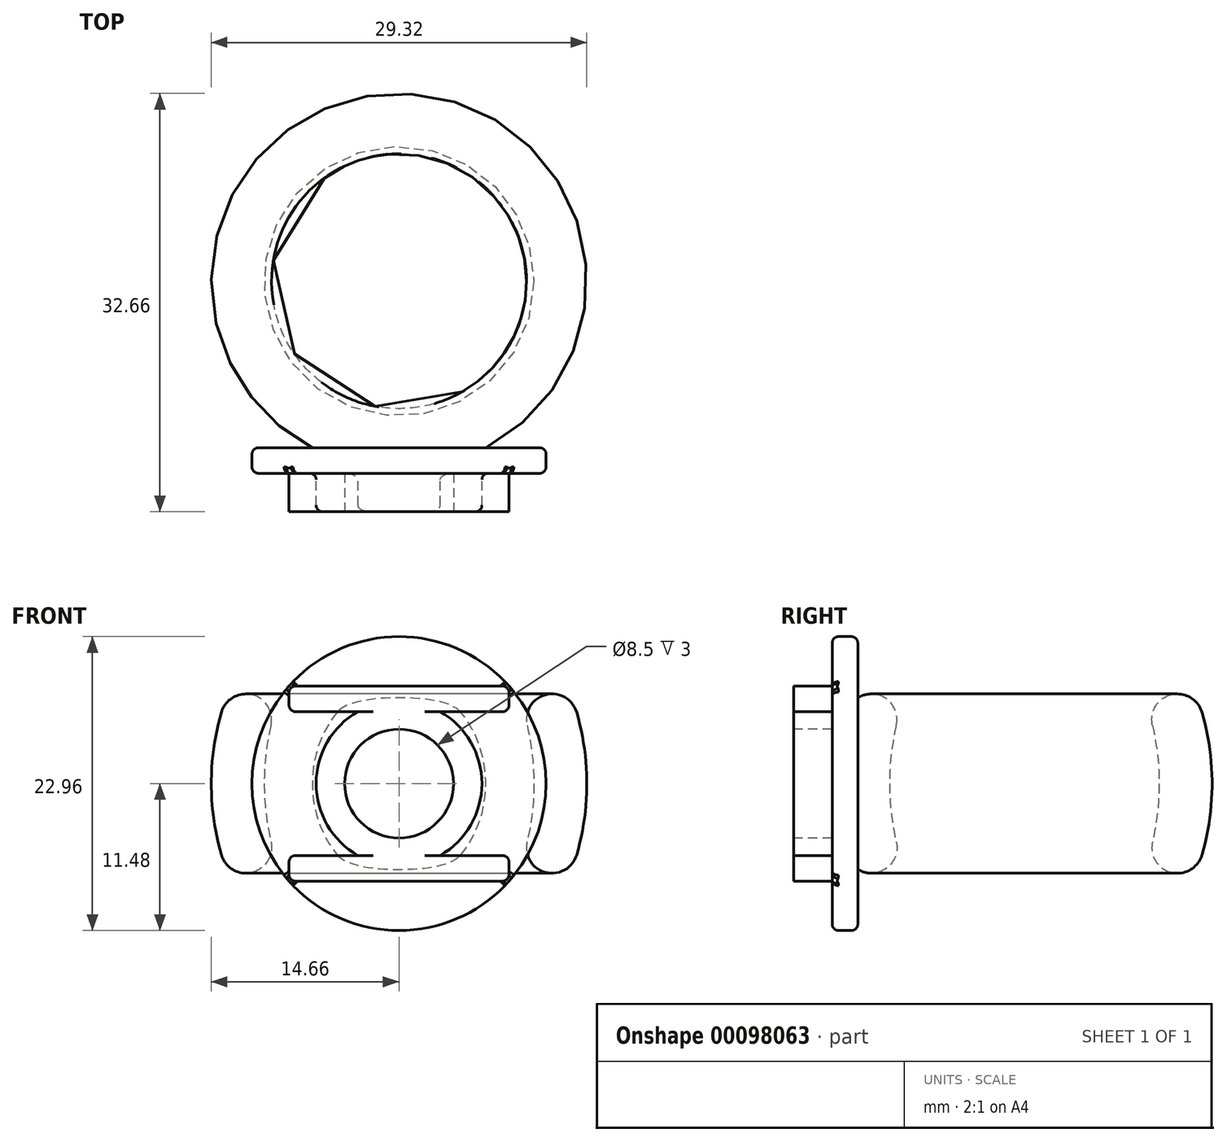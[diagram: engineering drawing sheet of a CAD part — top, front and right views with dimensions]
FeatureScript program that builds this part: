
annotation { "Feature Type Name" : "Feature", "Feature Type Description" : "" }
export const myFeature = defineFeature(function(context is Context, id is Id, definition is map)
    precondition{}
    {
        {
            var Q0;
            Q0=qCreatedBy(makeId("Front.planeOp"),FACE);
            var sketch = newSketch(context, id + "F0", { "sketchPlane" : qUnion([Q0])});
            skArc(sketch, "E0", {"start": v(10, -4.55) * mm, "mid": v(10.52, 0) * mm, "end": v(10, 4.55) * mm});
            skArc(sketch, "E1", {"start": v(13.87, 5.56) * mm, "mid": v(11.44, 6.94) * mm, "end": v(10, 4.55) * mm});
            skArc(sketch, "E2", {"start": v(13.87, -5.56) * mm, "mid": v(14.66, 0) * mm, "end": v(13.87, 5.56) * mm});
            skArc(sketch, "E3", {"start": v(10, -4.55) * mm, "mid": v(11.44, -6.94) * mm, "end": v(13.87, -5.56) * mm});
            skLineSegment(sketch, "E4", {"start": v(0, 27.13) * mm, "end": v(0, -21.84) * mm});
            skLineSegment(sketch, "E5", {"start": v(10, -4.55) * mm, "end": v(13.87, -5.56) * mm, "construction": true});
            skLineSegment(sketch, "E6", {"start": v(10, 4.55) * mm, "end": v(13.87, 5.56) * mm, "construction": true});
            skLineSegment(sketch, "E7", {"start": v(14.66, 0) * mm, "end": v(10.52, 0) * mm, "construction": true});
            skLineSegment(sketch, "E8", {"start": v(10.52, 0) * mm, "end": v(0, 0) * mm, "construction": true});
            skSolve(sketch);
        }
        {
            var Q0;
            Q0 = qSketchRegion(id + "F0", true);
            var Q1;
            Q1=sQuery(id+"F0.wireOp",EDGE,"E4");
            revolve(context, id + "F1", {"entities" : qUnion([Q0]), "axis" : qUnion([Q1]), "revolveType" : RevolveType.FULL});
        }
        {
            var Q0;
            Q0=qCreatedBy(makeId("Front.planeOp"),FACE);
            cPlane(context, id + "F2", {"entities" : qUnion([Q0]), "cplaneType" : CPlaneType.OFFSET, "offset" : 13 * mm, "width" : 150 * mm, "height" : 150 * mm});
        }
        {
            var Q0;
            Q0=qCreatedBy(id+"F2.planeOp",FACE);
            var sketch = newSketch(context, id + "F3", { "sketchPlane" : qUnion([Q0])});
            skCircle(sketch, "E9", {"center": v(0, 0) * mm, "radius": 11.48 * mm});
            skSolve(sketch);
        }
        {
            var Q0;
            Q0 = qSketchRegion(id + "F3", true);
            extrude(context, id + "F4", {"entities" : qUnion([Q0]), "operationType" : NewBodyOperationType.ADD, "depth" : 2 * mm});
        }
        {
            var Q0;
            Q0=makeQuery(id+"F4.opExtrude","CAP_FACE",FACE,{"disambiguationData":[OSD([sQuery(id+"F3.wireOp",EDGE,"E9")])],"isStart":false});
            var sketch = newSketch(context, id + "F5", { "sketchPlane" : qUnion([Q0])});
            skLineSegment(sketch, "E10", {"start": v(8.58, 7.62) * mm, "end": v(-8.58, 7.62) * mm});
            skPoint(sketch, "E11.endSnap0", {"position": v(0, 7.62) * mm});
            skCircle(sketch, "E12", {"center": v(0, 0) * mm, "radius": 6.47 * mm});
            skLineSegment(sketch, "E13.MirrorCS", {"start": v(8.58, -7.62) * mm, "end": v(-8.58, -7.62) * mm});
            skLineSegment(sketch, "E14", {"start": v(-8.58, 7.62) * mm, "end": v(-8.58, 5.62) * mm});
            skLineSegment(sketch, "E15.MirrorCS", {"start": v(8.58, 7.62) * mm, "end": v(8.58, 5.62) * mm});
            skLineSegment(sketch, "E16.MirrorCS", {"start": v(-8.58, -7.62) * mm, "end": v(-8.58, -5.62) * mm});
            skLineSegment(sketch, "E17.MirrorCS", {"start": v(8.58, -7.62) * mm, "end": v(8.58, -5.62) * mm});
            skLineSegment(sketch, "E18", {"start": v(-8.58, 5.62) * mm, "end": v(8.58, 5.62) * mm});
            skLineSegment(sketch, "E19.MirrorCS", {"start": v(-8.58, -5.62) * mm, "end": v(8.58, -5.62) * mm});
            skSolve(sketch);
        }
        {
            var Q0;
            Q0 = qSketchRegion(id + "F5", true);
            extrude(context, id + "F6", {"entities" : qUnion([Q0]), "operationType" : NewBodyOperationType.ADD, "depth" : 3 * mm});
        }
        {
            var Q0;
            Q0=makeQuery(id+"F6.opExtrude","CAP_FACE",FACE,{"disambiguationData":[OSD([sQuery(id+"F5.wireOp",EDGE,"E10"),sQuery(id+"F5.wireOp",EDGE,"E12"),sQuery(id+"F5.wireOp",EDGE,"E14"),sQuery(id+"F5.wireOp",EDGE,"E15.MirrorCS"),sQuery(id+"F5.wireOp",EDGE,"E13.MirrorCS"),sQuery(id+"F5.wireOp",EDGE,"E16.MirrorCS"),sQuery(id+"F5.wireOp",EDGE,"E17.MirrorCS"),sQuery(id+"F5.wireOp",EDGE,"E18"),sQuery(id+"F5.wireOp",EDGE,"E19.MirrorCS")])],"isStart":false});
            var sketch = newSketch(context, id + "F7", { "sketchPlane" : qUnion([Q0])});
            skCircle(sketch, "E20", {"center": v(0, 0) * mm, "radius": 4.25 * mm});
            skSolve(sketch);
        }
        {
            var Q0;
            Q0 = qSketchRegion(id + "F7", true);
            extrude(context, id + "F8", {"entities" : qUnion([Q0]), "operationType" : NewBodyOperationType.REMOVE, "oppositeDirection" : true, "depth" : 3 * mm});
        }
        {
            var Q0;
            Q0=makeQuery(id+"F6.opExtrude","SWEPT_EDGE",EDGE,{"disambiguationData":[OSD([sQuery(id+"F3.wireOp",EDGE,"E9"),sQuery(id+"F5.wireOp",EDGE,"E13.MirrorCS"),sQuery(id+"F5.wireOp",EDGE,"E16.MirrorCS")])]});
            var Q1;
            Q1=makeQuery(id+"F6.opExtrude","SWEPT_EDGE",EDGE,{"disambiguationData":[OSD([sQuery(id+"F5.wireOp",EDGE,"E16.MirrorCS"),sQuery(id+"F5.wireOp",EDGE,"E19.MirrorCS")])]});
            var Q2;
            Q2=makeQuery(id+"F6.opExtrude","SWEPT_EDGE",EDGE,{"disambiguationData":[OSD([sQuery(id+"F3.wireOp",EDGE,"E9"),sQuery(id+"F5.wireOp",EDGE,"E13.MirrorCS"),sQuery(id+"F5.wireOp",EDGE,"E17.MirrorCS")])]});
            var Q3;
            Q3=makeQuery(id+"F6.opExtrude","SWEPT_EDGE",EDGE,{"disambiguationData":[OSD([sQuery(id+"F5.wireOp",EDGE,"E17.MirrorCS"),sQuery(id+"F5.wireOp",EDGE,"E19.MirrorCS")])]});
            var Q4;
            Q4=makeQuery(id+"F6.opExtrude","SWEPT_EDGE",EDGE,{"disambiguationData":[OSD([sQuery(id+"F5.wireOp",EDGE,"E14"),sQuery(id+"F5.wireOp",EDGE,"E18")])]});
            var Q5;
            Q5=makeQuery(id+"F6.opExtrude","SWEPT_EDGE",EDGE,{"disambiguationData":[OSD([sQuery(id+"F3.wireOp",EDGE,"E9"),sQuery(id+"F5.wireOp",EDGE,"E10"),sQuery(id+"F5.wireOp",EDGE,"E14")])]});
            var Q6;
            Q6=makeQuery(id+"F6.opExtrude","SWEPT_EDGE",EDGE,{"disambiguationData":[OSD([sQuery(id+"F5.wireOp",EDGE,"E15.MirrorCS"),sQuery(id+"F5.wireOp",EDGE,"E18")])]});
            var Q7;
            Q7=makeQuery(id+"F6.opExtrude","SWEPT_EDGE",EDGE,{"disambiguationData":[OSD([sQuery(id+"F3.wireOp",EDGE,"E9"),sQuery(id+"F5.wireOp",EDGE,"E10"),sQuery(id+"F5.wireOp",EDGE,"E15.MirrorCS")])]});
            fillet(context, id + "F9", {"entities" : qUnion([Q0, Q1, Q2, Q3, Q4, Q5, Q6, Q7]), "radius" : .5 * mm, "tangentPropagation" : true, "allowEdgeOverflow" : false});
        }
        {
            var Q0;
            Q0=makeQuery(id+"F4.opExtrude","CAP_EDGE",EDGE,{"disambiguationData":[OSD([sQuery(id+"F3.wireOp",EDGE,"E9")])],"isStart":true});
            var Q1;
            {var subQ0=sQuery(id+"F3.wireOp",EDGE,"E9");Q1=makeQuery(id+"F6.boolean.opBoolean","SPLIT",EDGE,{"disambiguationData":[TD([makeQuery(id+"F4.opExtrude","SWEPT_FACE",FACE,{"disambiguationData":[OSD([subQ0])]}),makeQuery(id+"F4.opExtrude","CAP_FACE",FACE,{"disambiguationData":[OSD([subQ0])],"isStart":false}),makeQuery(id+"F6.opExtrude","SWEPT_FACE",FACE,{"disambiguationData":[OSD([sQuery(id+"F5.wireOp",EDGE,"E10")])]}),makeQuery(id+"F6.opExtrude","SWEPT_FACE",FACE,{"disambiguationData":[OSD([sQuery(id+"F5.wireOp",EDGE,"E14")])]}),makeQuery(id+"F6.opExtrude","SWEPT_FACE",FACE,{"disambiguationData":[OSD([sQuery(id+"F5.wireOp",EDGE,"E13.MirrorCS")])]}),makeQuery(id+"F6.opExtrude","SWEPT_FACE",FACE,{"disambiguationData":[OSD([sQuery(id+"F5.wireOp",EDGE,"E16.MirrorCS")])]})])],"derivedFrom":makeQuery(id+"F4.opExtrude","CAP_EDGE",EDGE,{"disambiguationData":[OSD([subQ0])],"isStart":false})});}
            var Q2;
            {var subQ0=sQuery(id+"F3.wireOp",EDGE,"E9");Q2=makeQuery(id+"F6.boolean.opBoolean","SPLIT",EDGE,{"disambiguationData":[TD([makeQuery(id+"F4.opExtrude","SWEPT_FACE",FACE,{"disambiguationData":[OSD([subQ0])]}),makeQuery(id+"F4.opExtrude","CAP_FACE",FACE,{"disambiguationData":[OSD([subQ0])],"isStart":false}),makeQuery(id+"F6.opExtrude","SWEPT_FACE",FACE,{"disambiguationData":[OSD([sQuery(id+"F5.wireOp",EDGE,"E10")])]}),makeQuery(id+"F6.opExtrude","SWEPT_FACE",FACE,{"disambiguationData":[OSD([sQuery(id+"F5.wireOp",EDGE,"E14")])]}),makeQuery(id+"F6.opExtrude","SWEPT_FACE",FACE,{"disambiguationData":[OSD([sQuery(id+"F5.wireOp",EDGE,"E15.MirrorCS")])]})])],"derivedFrom":makeQuery(id+"F4.opExtrude","CAP_EDGE",EDGE,{"disambiguationData":[OSD([subQ0])],"isStart":false})});}
            var Q3;
            {var subQ0=sQuery(id+"F3.wireOp",EDGE,"E9");Q3=makeQuery(id+"F6.boolean.opBoolean","SPLIT",EDGE,{"disambiguationData":[TD([makeQuery(id+"F4.opExtrude","SWEPT_FACE",FACE,{"disambiguationData":[OSD([subQ0])]}),makeQuery(id+"F4.opExtrude","CAP_FACE",FACE,{"disambiguationData":[OSD([subQ0])],"isStart":false}),makeQuery(id+"F6.opExtrude","SWEPT_FACE",FACE,{"disambiguationData":[OSD([sQuery(id+"F5.wireOp",EDGE,"E10")])]}),makeQuery(id+"F6.opExtrude","SWEPT_FACE",FACE,{"disambiguationData":[OSD([sQuery(id+"F5.wireOp",EDGE,"E15.MirrorCS")])]}),makeQuery(id+"F6.opExtrude","SWEPT_FACE",FACE,{"disambiguationData":[OSD([sQuery(id+"F5.wireOp",EDGE,"E13.MirrorCS")])]}),makeQuery(id+"F6.opExtrude","SWEPT_FACE",FACE,{"disambiguationData":[OSD([sQuery(id+"F5.wireOp",EDGE,"E17.MirrorCS")])]})])],"derivedFrom":makeQuery(id+"F4.opExtrude","CAP_EDGE",EDGE,{"disambiguationData":[OSD([subQ0])],"isStart":false})});}
            var Q4;
            {var subQ0=sQuery(id+"F3.wireOp",EDGE,"E9");Q4=makeQuery(id+"F6.boolean.opBoolean","SPLIT",EDGE,{"disambiguationData":[TD([makeQuery(id+"F4.opExtrude","SWEPT_FACE",FACE,{"disambiguationData":[OSD([subQ0])]}),makeQuery(id+"F4.opExtrude","CAP_FACE",FACE,{"disambiguationData":[OSD([subQ0])],"isStart":false}),makeQuery(id+"F6.opExtrude","SWEPT_FACE",FACE,{"disambiguationData":[OSD([sQuery(id+"F5.wireOp",EDGE,"E13.MirrorCS")])]}),makeQuery(id+"F6.opExtrude","SWEPT_FACE",FACE,{"disambiguationData":[OSD([sQuery(id+"F5.wireOp",EDGE,"E16.MirrorCS")])]}),makeQuery(id+"F6.opExtrude","SWEPT_FACE",FACE,{"disambiguationData":[OSD([sQuery(id+"F5.wireOp",EDGE,"E17.MirrorCS")])]})])],"derivedFrom":makeQuery(id+"F4.opExtrude","CAP_EDGE",EDGE,{"disambiguationData":[OSD([subQ0])],"isStart":false})});}
            fillet(context, id + "F10", {"entities" : qUnion([Q0, Q1, Q2, Q3, Q4]), "radius" : .5 * mm, "tangentPropagation" : true, "allowEdgeOverflow" : false});
        }
        {
            var Q0;
            {var subQ0=sQuery(id+"F5.wireOp",EDGE,"E12");Q0=makeQuery(id+"F6.opExtrude","CAP_EDGE",EDGE,{"disambiguationData":[OSD([subQ0]),TDD([makeQuery(id+"F5.imprint","IMPRINT",EDGE,{"disambiguationData":[TD([[makeQuery(id+"F5.imprint","INTERSECT",VERTEX,{"disambiguationData":[OD(0.0)],"derivedFrom":[subQ0,sQuery(id+"F5.wireOp",EDGE,"E18")]}),-1.0]])],"derivedFrom":subQ0})])],"isStart":false});}
            var Q1;
            {var subQ0=sQuery(id+"F5.wireOp",EDGE,"E12");Q1=makeQuery(id+"F6.opExtrude","CAP_EDGE",EDGE,{"disambiguationData":[OSD([subQ0]),TDD([makeQuery(id+"F5.imprint","IMPRINT",EDGE,{"disambiguationData":[TD([[makeQuery(id+"F5.imprint","INTERSECT",VERTEX,{"disambiguationData":[OD(0.0)],"derivedFrom":[subQ0,sQuery(id+"F5.wireOp",EDGE,"E18")]}),-1.0]])],"derivedFrom":subQ0})])],"isStart":true});}
            var Q2;
            {var subQ0=sQuery(id+"F5.wireOp",EDGE,"E12");Q2=makeQuery(id+"F6.opExtrude","CAP_EDGE",EDGE,{"disambiguationData":[OSD([subQ0]),TDD([makeQuery(id+"F5.imprint","IMPRINT",EDGE,{"disambiguationData":[TD([[makeQuery(id+"F5.imprint","INTERSECT",VERTEX,{"disambiguationData":[OD(1.0)],"derivedFrom":[subQ0,sQuery(id+"F5.wireOp",EDGE,"E18")]}),1.0]])],"derivedFrom":subQ0})])],"isStart":false});}
            var Q3;
            {var subQ0=sQuery(id+"F5.wireOp",EDGE,"E12");Q3=makeQuery(id+"F6.opExtrude","CAP_EDGE",EDGE,{"disambiguationData":[OSD([subQ0]),TDD([makeQuery(id+"F5.imprint","IMPRINT",EDGE,{"disambiguationData":[TD([[makeQuery(id+"F5.imprint","INTERSECT",VERTEX,{"disambiguationData":[OD(1.0)],"derivedFrom":[subQ0,sQuery(id+"F5.wireOp",EDGE,"E18")]}),1.0]])],"derivedFrom":subQ0})])],"isStart":true});}
            fillet(context, id + "F11", {"entities" : qUnion([Q0, Q1, Q2, Q3]), "radius" : .5 * mm, "tangentPropagation" : true, "allowEdgeOverflow" : false});
        }
    });
